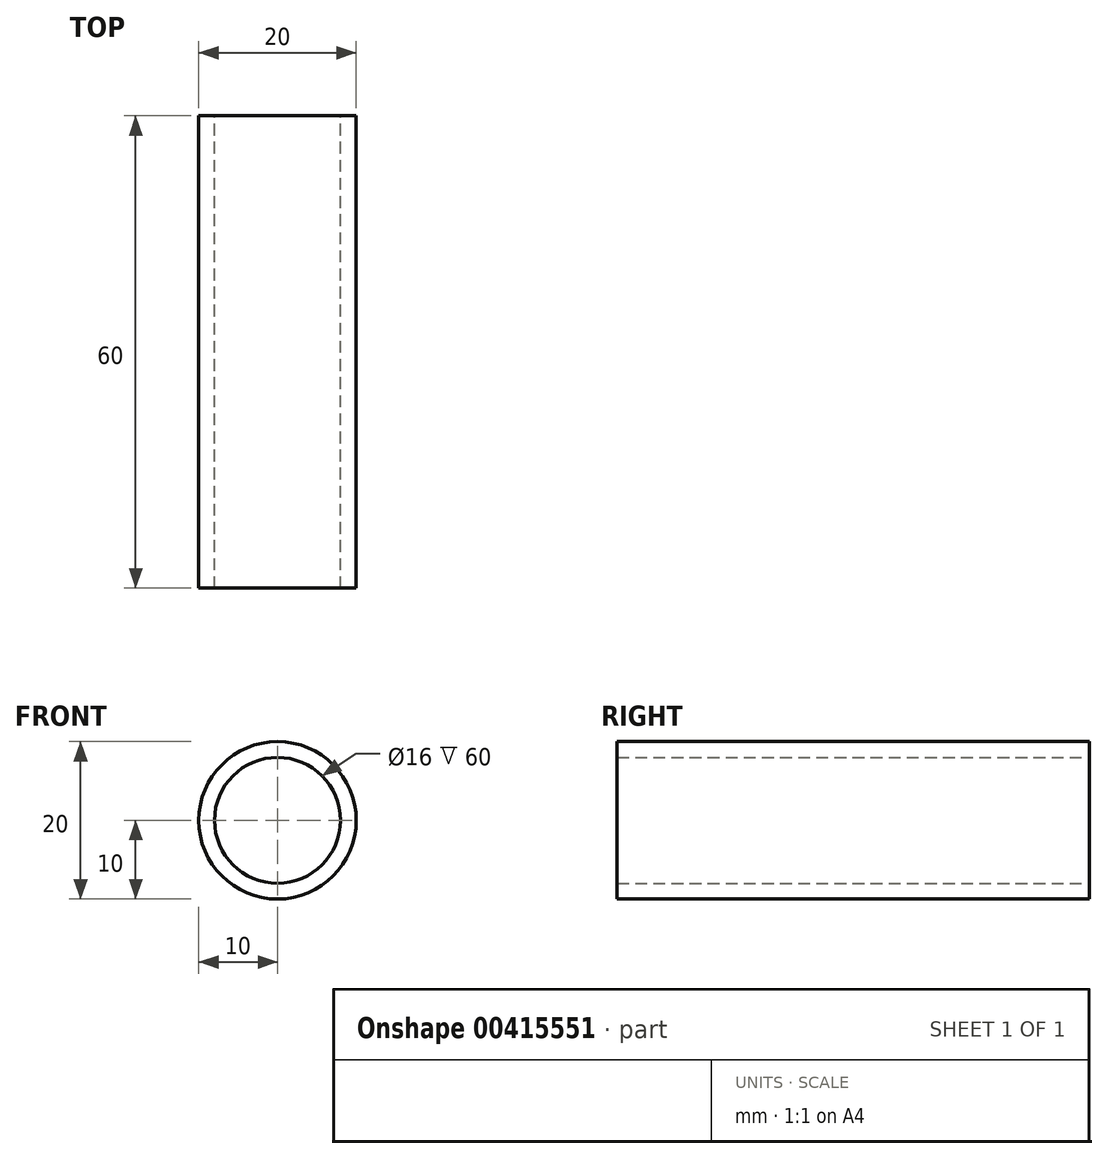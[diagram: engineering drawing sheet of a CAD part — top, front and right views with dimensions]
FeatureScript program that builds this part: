
annotation { "Feature Type Name" : "Feature", "Feature Type Description" : "" }
export const myFeature = defineFeature(function(context is Context, id is Id, definition is map)
    precondition{}
    {
        {
            var Q0;
            Q0=qCreatedBy(makeId("Front.planeOp"),FACE);
            var sketch = newSketch(context, id + "F0", { "sketchPlane" : qUnion([Q0])});
            skCircle(sketch, "E0", {"center": v(0, 0) * mm, "radius": 8 * mm});
            skCircle(sketch, "E1", {"center": v(0, 0) * mm, "radius": 10 * mm});
            skSolve(sketch);
        }
        {
            var Q0;
            Q0=makeQuery(id+"F0.imprint","IMPRINT",FACE,{"disambiguationData":[TD([[makeQuery(id+"F0.imprint","IMPRINT",EDGE,{"derivedFrom":sQuery(id+"F0.wireOp",EDGE,"E0")}),-1.0]])]});
            extrude(context, id + "F1", {"entities" : qUnion([Q0]), "depth" : 60 * mm});
        }
    });
